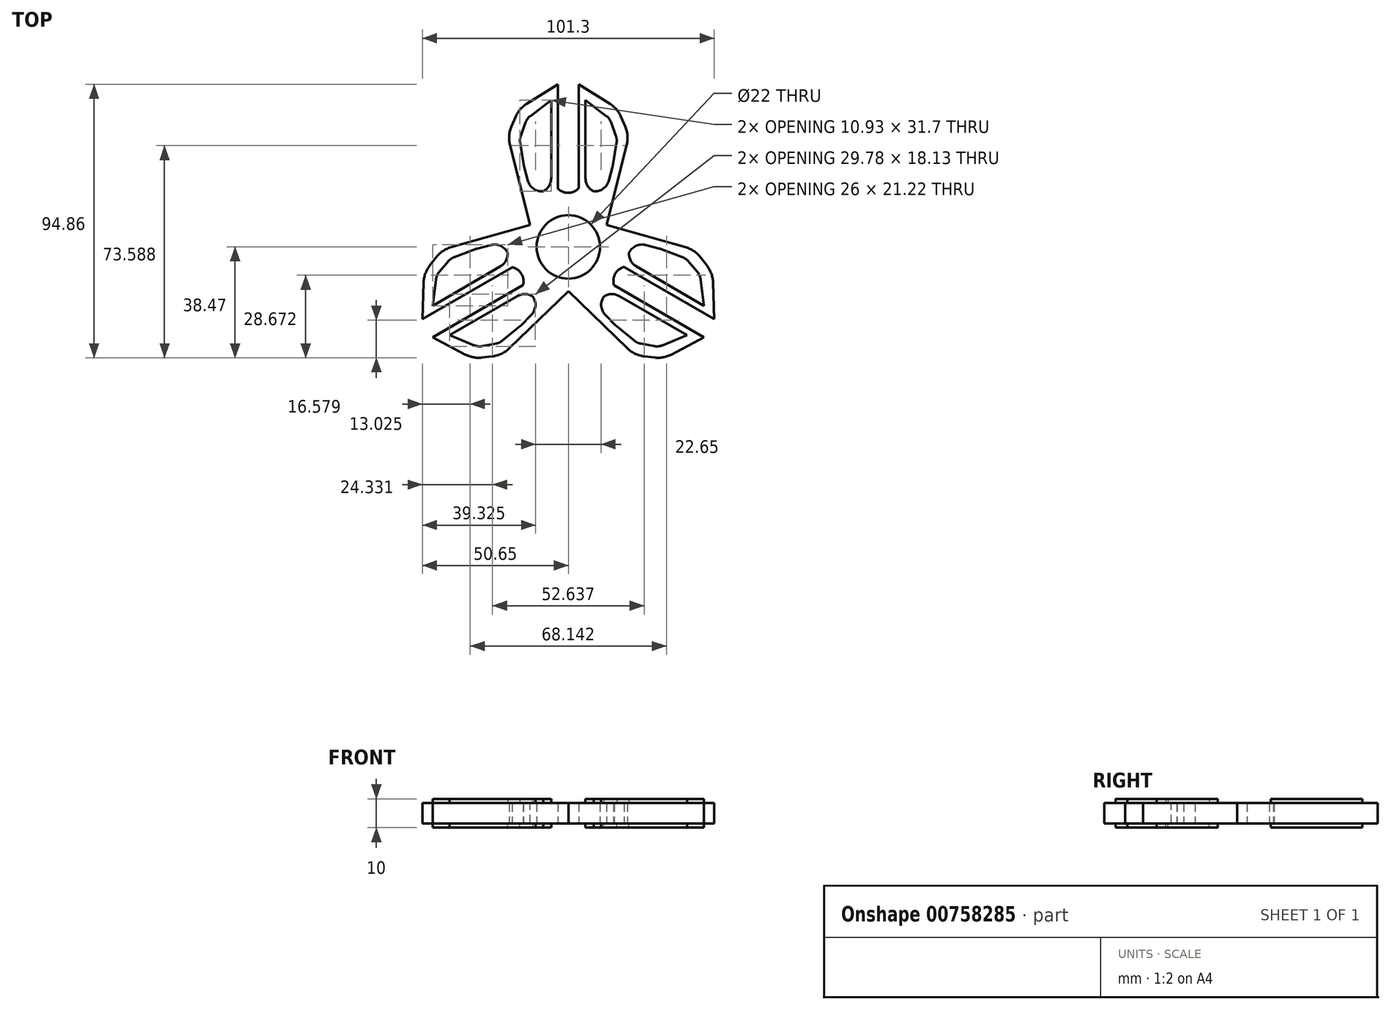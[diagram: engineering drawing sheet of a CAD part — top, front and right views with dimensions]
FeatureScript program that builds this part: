
annotation { "Feature Type Name" : "Feature", "Feature Type Description" : "" }
export const myFeature = defineFeature(function(context is Context, id is Id, definition is map)
    precondition{}
    {
        {
            var Q0;
            Q0=qCreatedBy(makeId("Top.planeOp"),FACE);
            var sketch = newSketch(context, id + "F0", { "sketchPlane" : qUnion([Q0])});
            skCircle(sketch, "E0", {"center": v(0, 0) * mm, "radius": 11 * mm});
            skLineSegment(sketch, "E1", {"start": v(3.63, 10.38) * mm, "end": v(3.63, 56.39) * mm});
            skLineSegment(sketch, "E2", {"start": v(3.63, 56.39) * mm, "end": v(17.02, 48.05) * mm});
            skLineSegment(sketch, "E3", {"start": v(17.02, 48.05) * mm, "end": v(21.06, 38.7) * mm});
            skLineSegment(sketch, "E4", {"start": v(21.06, 38.7) * mm, "end": v(15.78, 17.67) * mm});
            skLineSegment(sketch, "E5", {"start": v(15.78, 17.67) * mm, "end": v(15.78, 17.67) * mm});
            skLineSegment(sketch, "E6", {"start": v(15.78, 17.67) * mm, "end": v(13.08, 6.92) * mm});
            skLineSegment(sketch, "E7", {"start": v(13.08, 6.92) * mm, "end": v(9.95, 4.7) * mm});
            skLineSegment(sketch, "E8.MirrorCS", {"start": v(-15.78, 17.67) * mm, "end": v(-15.78, 17.67) * mm});
            skLineSegment(sketch, "E9.MirrorCS", {"start": v(-3.63, 56.39) * mm, "end": v(-17.02, 48.05) * mm});
            skLineSegment(sketch, "E10.MirrorCS", {"start": v(-15.78, 17.67) * mm, "end": v(-13.08, 6.92) * mm});
            skLineSegment(sketch, "E11.MirrorCS", {"start": v(-21.06, 38.7) * mm, "end": v(-15.78, 17.67) * mm});
            skLineSegment(sketch, "E12.MirrorCS", {"start": v(-17.02, 48.05) * mm, "end": v(-21.06, 38.7) * mm});
            skLineSegment(sketch, "E13.MirrorCS", {"start": v(-3.63, 10.38) * mm, "end": v(-3.63, 56.39) * mm});
            skLineSegment(sketch, "E14.MirrorCS", {"start": v(-13.08, 6.92) * mm, "end": v(-9.95, 4.7) * mm});
            skLineSegment(sketch, "E15", {"start": v(5.86, 50.97) * mm, "end": v(14.38, 44.5) * mm});
            skLineSegment(sketch, "E16", {"start": v(14.38, 44.5) * mm, "end": v(16.93, 37.35) * mm});
            skLineSegment(sketch, "E17", {"start": v(16.93, 37.35) * mm, "end": v(15.4, 27.98) * mm});
            skLineSegment(sketch, "E18", {"start": v(15.4, 27.98) * mm, "end": v(12.67, 18.1) * mm});
            skLineSegment(sketch, "E19", {"start": v(12.67, 18.1) * mm, "end": v(5.98, 19.95) * mm});
            skLineSegment(sketch, "E20", {"start": v(5.98, 19.95) * mm, "end": v(5.86, 50.97) * mm});
            skLineSegment(sketch, "E21.MirrorCS", {"start": v(-15.4, 27.98) * mm, "end": v(-12.67, 18.1) * mm});
            skLineSegment(sketch, "E22.MirrorCS", {"start": v(-5.98, 19.95) * mm, "end": v(-5.86, 50.97) * mm});
            skLineSegment(sketch, "E23.MirrorCS", {"start": v(-12.67, 18.1) * mm, "end": v(-5.98, 19.95) * mm});
            skLineSegment(sketch, "E24.MirrorCS", {"start": v(-5.86, 50.97) * mm, "end": v(-14.38, 44.5) * mm});
            skLineSegment(sketch, "E25.MirrorCS", {"start": v(-14.38, 44.5) * mm, "end": v(-16.93, 37.35) * mm});
            skLineSegment(sketch, "E26.MirrorCS", {"start": v(-16.93, 37.35) * mm, "end": v(-15.4, 27.98) * mm});
            skCircle(sketch, "E27.0", {"center": v(0, 0) * mm, "radius": 14 * mm});
            skLineSegment(sketch, "E28", {"start": v(3.63, 20.22) * mm, "end": v(0, 14) * mm});
            skLineSegment(sketch, "E29", {"start": v(0, 14) * mm, "end": v(-3.63, 20.22) * mm});
            skSolve(sketch);
        }
        {
            var Q0;
            {var subQ2=sQuery(id+"F0.wireOp",EDGE,"E14.MirrorCS");Q0=makeQuery(id+"F0.imprint","IMPRINT",FACE,{"disambiguationData":[TD([[makeQuery(id+"F0.imprint","IMPRINT",EDGE,{"derivedFrom":subQ2}),1.0]])]});}
            var Q1;
            Q1=makeQuery(id+"F0.imprint","IMPRINT",FACE,{"disambiguationData":[TD([[makeQuery(id+"F0.imprint","IMPRINT",EDGE,{"derivedFrom":sQuery(id+"F0.wireOp",EDGE,"E3")}),-1.0]])]});
            var Q2;
            {var subQ0=sQuery(id+"F0.wireOp",EDGE,"E0");var subQ1=sQuery(id+"F0.wireOp",EDGE,"E7");var subQ2=makeQuery(id+"F0.imprint","INTERSECT",VERTEX,{"derivedFrom":[subQ1,subQ0]});Q2=makeQuery(id+"F0.imprint","IMPRINT",FACE,{"disambiguationData":[TD([[makeQuery(id+"F0.imprint","IMPRINT",EDGE,{"disambiguationData":[TD([[subQ2,1.0]])],"derivedFrom":subQ1}),1.0]])]});}
            var Q3;
            {var subQ0=sQuery(id+"F0.wireOp",EDGE,"E0");var subQ1=sQuery(id+"F0.wireOp",EDGE,"E7");var subQ2=makeQuery(id+"F0.imprint","INTERSECT",VERTEX,{"derivedFrom":[subQ1,subQ0]});Q3=makeQuery(id+"F0.imprint","IMPRINT",FACE,{"disambiguationData":[TD([[makeQuery(id+"F0.imprint","IMPRINT",EDGE,{"disambiguationData":[TD([[subQ2,1.0]])],"derivedFrom":subQ1}),-1.0]])]});}
            var Q4;
            {var subQ0=sQuery(id+"F0.wireOp",EDGE,"E13.MirrorCS");var subQ1=sQuery(id+"F0.wireOp",EDGE,"E0");var subQ2=makeQuery(id+"F0.imprint","INTERSECT",VERTEX,{"derivedFrom":[subQ1,subQ0]});Q4=makeQuery(id+"F0.imprint","IMPRINT",FACE,{"disambiguationData":[TD([[makeQuery(id+"F0.imprint","IMPRINT",EDGE,{"disambiguationData":[TD([[subQ2,1.0]])],"derivedFrom":subQ1}),-1.0]])]});}
            var Q5;
            Q5=makeQuery(id+"F0.imprint","IMPRINT",FACE,{"disambiguationData":[TD([[makeQuery(id+"F0.imprint","IMPRINT",EDGE,{"derivedFrom":sQuery(id+"F0.wireOp",EDGE,"E21.MirrorCS")}),-1.0]])]});
            var Q6;
            {var subQ0=sQuery(id+"F0.wireOp",EDGE,"E28");Q6=makeQuery(id+"F0.imprint","IMPRINT",FACE,{"disambiguationData":[TD([[makeQuery(id+"F0.imprint","IMPRINT",EDGE,{"derivedFrom":subQ0}),1.0]])]});}
            var Q7;
            {var subQ0=sQuery(id+"F0.wireOp",EDGE,"E29");Q7=makeQuery(id+"F0.imprint","IMPRINT",FACE,{"disambiguationData":[TD([[makeQuery(id+"F0.imprint","IMPRINT",EDGE,{"derivedFrom":subQ0}),1.0]])]});}
            extrude(context, id + "F1", {"entities" : qUnion([Q0, Q1, Q2, Q3, Q4, Q5, Q6, Q7]), "depth" : 3.5 * mm, "offsetDistance" : 25 * mm});
        }
        {
            var Q0;
            Q0=makeQuery(id+"F0.imprint","IMPRINT",FACE,{"disambiguationData":[TD([[makeQuery(id+"F0.imprint","IMPRINT",EDGE,{"derivedFrom":sQuery(id+"F0.wireOp",EDGE,"E15")}),-1.0]])]});
            var Q1;
            Q1=makeQuery(id+"F0.imprint","IMPRINT",FACE,{"disambiguationData":[TD([[makeQuery(id+"F0.imprint","IMPRINT",EDGE,{"derivedFrom":sQuery(id+"F0.wireOp",EDGE,"E21.MirrorCS")}),1.0]])]});
            extrude(context, id + "F2", {"entities" : qUnion([Q0, Q1]), "operationType" : NewBodyOperationType.ADD, "depth" : 5 * mm, "offsetDistance" : 25 * mm});
        }
        {
            var Q0;
            Q0=makeQuery(id+"F1.opExtrude","SWEPT_EDGE",EDGE,{"disambiguationData":[OSD([sQuery(id+"F0.wireOp",EDGE,"E3"),sQuery(id+"F0.wireOp",EDGE,"E2")])]});
            var Q1;
            Q1=makeQuery(id+"F1.opExtrude","SWEPT_EDGE",EDGE,{"disambiguationData":[OSD([sQuery(id+"F0.wireOp",EDGE,"E3"),sQuery(id+"F0.wireOp",EDGE,"E4")])]});
            var Q2;
            Q2=makeQuery(id+"F1.opExtrude","SWEPT_EDGE",EDGE,{"disambiguationData":[OSD([sQuery(id+"F0.wireOp",EDGE,"E12.MirrorCS"),sQuery(id+"F0.wireOp",EDGE,"E9.MirrorCS")])]});
            var Q3;
            Q3=makeQuery(id+"F1.opExtrude","SWEPT_EDGE",EDGE,{"disambiguationData":[OSD([sQuery(id+"F0.wireOp",EDGE,"E12.MirrorCS"),sQuery(id+"F0.wireOp",EDGE,"E11.MirrorCS")])]});
            fillet(context, id + "F3", {"entities" : qUnion([Q0, Q1, Q2, Q3]), "radius" : 10 * mm, "tangentPropagation" : true, "allowEdgeOverflow" : false});
        }
        {
            var Q0;
            {var subQ0=sQuery(id+"F0.wireOp",EDGE,"E20");var subQ1=sQuery(id+"F0.wireOp",EDGE,"E19");var subQ2=sQuery(id+"F0.wireOp",EDGE,"E18");var subQ3=sQuery(id+"F0.wireOp",EDGE,"E17");var subQ4=sQuery(id+"F0.wireOp",EDGE,"E16");var subQ5=sQuery(id+"F0.wireOp",EDGE,"E15");Q0=makeQuery(id+"F2.boolean.opBoolean","SPLIT",EDGE,{"disambiguationData":[TD([makeQuery(id+"F2.opExtrude","CAP_FACE",FACE,{"disambiguationData":[OSD([subQ5,subQ4,subQ3,subQ2,subQ1,subQ0])],"isStart":false})])],"derivedFrom":makeQuery(id+"F2.opExtrude","SWEPT_EDGE",EDGE,{"disambiguationData":[OSD([subQ5,subQ4])]})});}
            var Q1;
            {var subQ0=sQuery(id+"F0.wireOp",EDGE,"E20");var subQ1=sQuery(id+"F0.wireOp",EDGE,"E19");var subQ2=sQuery(id+"F0.wireOp",EDGE,"E18");var subQ3=sQuery(id+"F0.wireOp",EDGE,"E17");var subQ4=sQuery(id+"F0.wireOp",EDGE,"E16");var subQ5=sQuery(id+"F0.wireOp",EDGE,"E15");Q1=makeQuery(id+"F2.boolean.opBoolean","SPLIT",EDGE,{"disambiguationData":[TD([makeQuery(id+"F2.opExtrude","CAP_FACE",FACE,{"disambiguationData":[OSD([subQ5,subQ4,subQ3,subQ2,subQ1,subQ0])],"isStart":false})])],"derivedFrom":makeQuery(id+"F2.opExtrude","SWEPT_EDGE",EDGE,{"disambiguationData":[OSD([subQ4,subQ3])]})});}
            var Q2;
            {var subQ0=sQuery(id+"F0.wireOp",EDGE,"E20");var subQ1=sQuery(id+"F0.wireOp",EDGE,"E19");var subQ2=sQuery(id+"F0.wireOp",EDGE,"E18");var subQ3=sQuery(id+"F0.wireOp",EDGE,"E17");var subQ4=sQuery(id+"F0.wireOp",EDGE,"E16");var subQ5=sQuery(id+"F0.wireOp",EDGE,"E15");Q2=makeQuery(id+"F2.boolean.opBoolean","SPLIT",EDGE,{"disambiguationData":[TD([makeQuery(id+"F2.opExtrude","CAP_FACE",FACE,{"disambiguationData":[OSD([subQ5,subQ4,subQ3,subQ2,subQ1,subQ0])],"isStart":false})])],"derivedFrom":makeQuery(id+"F2.opExtrude","SWEPT_EDGE",EDGE,{"disambiguationData":[OSD([subQ3,subQ2])]})});}
            var Q3;
            {var subQ0=sQuery(id+"F0.wireOp",EDGE,"E26.MirrorCS");var subQ1=sQuery(id+"F0.wireOp",EDGE,"E25.MirrorCS");var subQ2=sQuery(id+"F0.wireOp",EDGE,"E24.MirrorCS");var subQ3=sQuery(id+"F0.wireOp",EDGE,"E23.MirrorCS");var subQ4=sQuery(id+"F0.wireOp",EDGE,"E22.MirrorCS");var subQ5=sQuery(id+"F0.wireOp",EDGE,"E21.MirrorCS");Q3=makeQuery(id+"F2.boolean.opBoolean","SPLIT",EDGE,{"disambiguationData":[TD([makeQuery(id+"F2.opExtrude","CAP_FACE",FACE,{"disambiguationData":[OSD([subQ5,subQ4,subQ3,subQ2,subQ1,subQ0])],"isStart":false})])],"derivedFrom":makeQuery(id+"F2.opExtrude","SWEPT_EDGE",EDGE,{"disambiguationData":[OSD([subQ5,subQ0])]})});}
            var Q4;
            {var subQ0=sQuery(id+"F0.wireOp",EDGE,"E26.MirrorCS");var subQ1=sQuery(id+"F0.wireOp",EDGE,"E25.MirrorCS");var subQ2=sQuery(id+"F0.wireOp",EDGE,"E24.MirrorCS");var subQ3=sQuery(id+"F0.wireOp",EDGE,"E23.MirrorCS");var subQ4=sQuery(id+"F0.wireOp",EDGE,"E22.MirrorCS");var subQ5=sQuery(id+"F0.wireOp",EDGE,"E21.MirrorCS");Q4=makeQuery(id+"F2.boolean.opBoolean","SPLIT",EDGE,{"disambiguationData":[TD([makeQuery(id+"F2.opExtrude","CAP_FACE",FACE,{"disambiguationData":[OSD([subQ5,subQ4,subQ3,subQ2,subQ1,subQ0])],"isStart":false})])],"derivedFrom":makeQuery(id+"F2.opExtrude","SWEPT_EDGE",EDGE,{"disambiguationData":[OSD([subQ1,subQ0])]})});}
            var Q5;
            {var subQ0=sQuery(id+"F0.wireOp",EDGE,"E26.MirrorCS");var subQ1=sQuery(id+"F0.wireOp",EDGE,"E25.MirrorCS");var subQ2=sQuery(id+"F0.wireOp",EDGE,"E24.MirrorCS");var subQ3=sQuery(id+"F0.wireOp",EDGE,"E23.MirrorCS");var subQ4=sQuery(id+"F0.wireOp",EDGE,"E22.MirrorCS");var subQ5=sQuery(id+"F0.wireOp",EDGE,"E21.MirrorCS");Q5=makeQuery(id+"F2.boolean.opBoolean","SPLIT",EDGE,{"disambiguationData":[TD([makeQuery(id+"F2.opExtrude","CAP_FACE",FACE,{"disambiguationData":[OSD([subQ5,subQ4,subQ3,subQ2,subQ1,subQ0])],"isStart":false})])],"derivedFrom":makeQuery(id+"F2.opExtrude","SWEPT_EDGE",EDGE,{"disambiguationData":[OSD([subQ2,subQ1])]})});}
            fillet(context, id + "F4", {"entities" : qUnion([Q0, Q1, Q2, Q3, Q4, Q5]), "radius" : 5 * mm, "tangentPropagation" : true, "allowEdgeOverflow" : false});
        }
        {
            var Q0;
            Q0=makeQuery(id+"F2.opExtrude","SWEPT_EDGE",EDGE,{"disambiguationData":[OSD([sQuery(id+"F0.wireOp",EDGE,"E21.MirrorCS"),sQuery(id+"F0.wireOp",EDGE,"E23.MirrorCS")])]});
            var Q1;
            Q1=makeQuery(id+"F2.opExtrude","SWEPT_EDGE",EDGE,{"disambiguationData":[OSD([sQuery(id+"F0.wireOp",EDGE,"E18"),sQuery(id+"F0.wireOp",EDGE,"E19")])]});
            var Q2;
            Q2=makeQuery(id+"F2.opExtrude","SWEPT_EDGE",EDGE,{"disambiguationData":[OSD([sQuery(id+"F0.wireOp",EDGE,"E22.MirrorCS"),sQuery(id+"F0.wireOp",EDGE,"E23.MirrorCS")])]});
            var Q3;
            Q3=makeQuery(id+"F2.opExtrude","SWEPT_EDGE",EDGE,{"disambiguationData":[OSD([sQuery(id+"F0.wireOp",EDGE,"E19"),sQuery(id+"F0.wireOp",EDGE,"E20")])]});
            fillet(context, id + "F5", {"entities" : qUnion([Q0, Q1, Q2, Q3]), "radius" : 5 * mm, "tangentPropagation" : true, "allowEdgeOverflow" : false});
        }
        {
            var Q0;
            {var subQ0=makeQuery(id+"F1.opExtrude","SWEPT_EDGE",EDGE,{"disambiguationData":[OSD([sQuery(id+"F0.wireOp",EDGE,"E27.0"),sQuery(id+"F0.wireOp",EDGE,"E28"),sQuery(id+"F0.wireOp",EDGE,"E29")])]});Q0=makeQuery(id+"F7.boolean.opBoolean","MERGE",EDGE,{"derivedFrom":[subQ0,makeQuery(id+"F7.opPattern","COPY",EDGE,{"derivedFrom":subQ0,"instanceName":"1"})]});}
            fillet(context, id + "F6", {"entities" : qUnion([Q0]), "radius" : 5 * mm, "tangentPropagation" : true, "allowEdgeOverflow" : false});
        }
        {
            var Q0;
            Q0=makeQuery(id+"F1.opExtrude","SWEPT_BODY",BODY,{"disambiguationData":[OSD([sQuery(id+"F0.wireOp",EDGE,"E3"),sQuery(id+"F0.wireOp",EDGE,"E4"),sQuery(id+"F0.wireOp",EDGE,"E6"),sQuery(id+"F0.wireOp",EDGE,"E7"),sQuery(id+"F0.wireOp",EDGE,"E15"),sQuery(id+"F0.wireOp",EDGE,"E16"),sQuery(id+"F0.wireOp",EDGE,"E17"),sQuery(id+"F0.wireOp",EDGE,"E18"),sQuery(id+"F0.wireOp",EDGE,"E19"),sQuery(id+"F0.wireOp",EDGE,"E20"),sQuery(id+"F0.wireOp",EDGE,"E2"),sQuery(id+"F0.wireOp",EDGE,"E14.MirrorCS"),sQuery(id+"F0.wireOp",EDGE,"E21.MirrorCS"),sQuery(id+"F0.wireOp",EDGE,"E22.MirrorCS"),sQuery(id+"F0.wireOp",EDGE,"E23.MirrorCS"),sQuery(id+"F0.wireOp",EDGE,"E24.MirrorCS"),sQuery(id+"F0.wireOp",EDGE,"E0"),sQuery(id+"F0.wireOp",EDGE,"E12.MirrorCS"),sQuery(id+"F0.wireOp",EDGE,"E13.MirrorCS"),sQuery(id+"F0.wireOp",EDGE,"E9.MirrorCS"),sQuery(id+"F0.wireOp",EDGE,"E11.MirrorCS"),sQuery(id+"F0.wireOp",EDGE,"E10.MirrorCS"),sQuery(id+"F0.wireOp",EDGE,"E25.MirrorCS"),sQuery(id+"F0.wireOp",EDGE,"E1"),sQuery(id+"F0.wireOp",EDGE,"E26.MirrorCS"),sQuery(id+"F0.wireOp",EDGE,"E27.0")])]});
            var Q1;
            Q1=qCreatedBy(makeId("Top.planeOp"),FACE);
            mirror(context, id + "F7", {"operationType" : NewBodyOperationType.ADD, "entities" : qUnion([Q0]), "mirrorPlane" : qUnion([Q1])});
        }
        {
            var Q0;
            Q0=makeQuery(id+"F1.opExtrude","SWEPT_BODY",BODY,{"disambiguationData":[OSD([sQuery(id+"F0.wireOp",EDGE,"E3"),sQuery(id+"F0.wireOp",EDGE,"E4"),sQuery(id+"F0.wireOp",EDGE,"E6"),sQuery(id+"F0.wireOp",EDGE,"E7"),sQuery(id+"F0.wireOp",EDGE,"E15"),sQuery(id+"F0.wireOp",EDGE,"E16"),sQuery(id+"F0.wireOp",EDGE,"E17"),sQuery(id+"F0.wireOp",EDGE,"E18"),sQuery(id+"F0.wireOp",EDGE,"E19"),sQuery(id+"F0.wireOp",EDGE,"E20"),sQuery(id+"F0.wireOp",EDGE,"E2"),sQuery(id+"F0.wireOp",EDGE,"E14.MirrorCS"),sQuery(id+"F0.wireOp",EDGE,"E21.MirrorCS"),sQuery(id+"F0.wireOp",EDGE,"E22.MirrorCS"),sQuery(id+"F0.wireOp",EDGE,"E23.MirrorCS"),sQuery(id+"F0.wireOp",EDGE,"E24.MirrorCS"),sQuery(id+"F0.wireOp",EDGE,"E0"),sQuery(id+"F0.wireOp",EDGE,"E12.MirrorCS"),sQuery(id+"F0.wireOp",EDGE,"E13.MirrorCS"),sQuery(id+"F0.wireOp",EDGE,"E9.MirrorCS"),sQuery(id+"F0.wireOp",EDGE,"E11.MirrorCS"),sQuery(id+"F0.wireOp",EDGE,"E10.MirrorCS"),sQuery(id+"F0.wireOp",EDGE,"E25.MirrorCS"),sQuery(id+"F0.wireOp",EDGE,"E1"),sQuery(id+"F0.wireOp",EDGE,"E26.MirrorCS"),sQuery(id+"F0.wireOp",EDGE,"E27.0")])]});
            var Q1;
            Q1=makeQuery(id+"F1.opExtrude","CAP_EDGE",EDGE,{"disambiguationData":[OSD([sQuery(id+"F0.wireOp",EDGE,"E0")])],"isStart":false});
            circularPattern(context, id + "F8", {"operationType" : NewBodyOperationType.ADD, "entities" : qUnion([Q0]), "axis" : qUnion([Q1]), "angle" : 360 * degree, "instanceCount" : 3, "equalSpace" : true});
        }
    });
